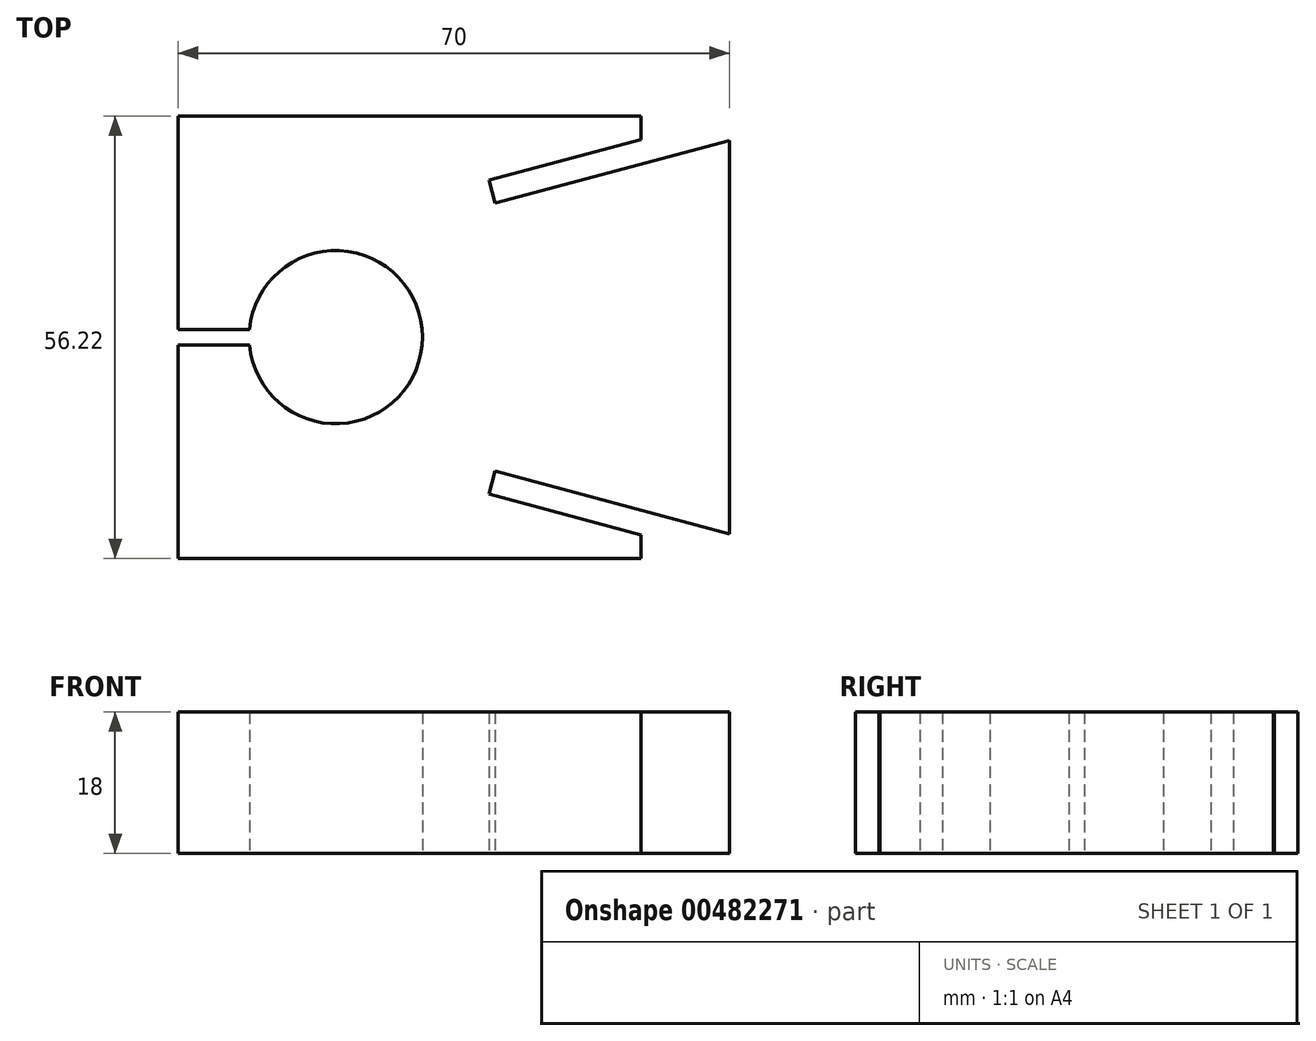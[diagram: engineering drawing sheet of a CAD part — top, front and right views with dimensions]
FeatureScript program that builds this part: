
annotation { "Feature Type Name" : "Feature", "Feature Type Description" : "" }
export const myFeature = defineFeature(function(context is Context, id is Id, definition is map)
    precondition{}
    {
        {
            var Q0;
            Q0=qCreatedBy(makeId("Top.planeOp"),FACE);
            var sketch = newSketch(context, id + "F0", { "sketchPlane" : qUnion([Q0])});
            skLineSegment(sketch, "E0", {"start": v(-70, 1) * mm, "end": v(-70, 28.1) * mm});
            skLineSegment(sketch, "E1", {"start": v(-70, 28.1) * mm, "end": v(-11.2, 28.1) * mm});
            skLineSegment(sketch, "E2", {"start": v(-11.2, 25.1) * mm, "end": v(-30.51, 19.93) * mm});
            skLineSegment(sketch, "E3", {"start": v(-30.51, 19.93) * mm, "end": v(-29.74, 17.03) * mm});
            skLineSegment(sketch, "E4", {"start": v(-29.74, 17.03) * mm, "end": v(0, 25) * mm});
            skLineSegment(sketch, "E5", {"start": v(0, 25) * mm, "end": v(0, 0) * mm});
            skLineSegment(sketch, "E6.MirrorCS", {"start": v(0, -25) * mm, "end": v(0, 0) * mm});
            skLineSegment(sketch, "E7.MirrorCS", {"start": v(-70, -1) * mm, "end": v(-70, -28.1) * mm});
            skLineSegment(sketch, "E8.MirrorCS", {"start": v(-29.74, -17.03) * mm, "end": v(0, -25) * mm});
            skLineSegment(sketch, "E9.MirrorCS", {"start": v(-70, -28.1) * mm, "end": v(-11.2, -28.1) * mm});
            skLineSegment(sketch, "E10.MirrorCS", {"start": v(-30.51, -19.93) * mm, "end": v(-29.74, -17.03) * mm});
            skLineSegment(sketch, "E11.MirrorCS", {"start": v(-11.2, -25.1) * mm, "end": v(-30.51, -19.93) * mm});
            skLineSegment(sketch, "E12", {"start": v(-11.2, 28.1) * mm, "end": v(-11.2, 25.1) * mm});
            skPoint(sketch, "E13.orphan", {"position": v(0, 28.1) * mm});
            skLineSegment(sketch, "E14.trimOffspring", {"start": v(-11.2, -25.1) * mm, "end": v(-11.2, -28.1) * mm});
            skPoint(sketch, "E15.orphan", {"position": v(0, -28.1) * mm});
            skArc(sketch, "E16", {"start": v(-60.95, -1) * mm, "mid": v(-39, 0) * mm, "end": v(-60.95, 1) * mm});
            skLineSegment(sketch, "E17.bottom", {"start": v(-60.95, 1) * mm, "end": v(-70, 1) * mm});
            skLineSegment(sketch, "E17.top", {"start": v(-60.95, -1) * mm, "end": v(-70, -1) * mm});
            skPoint(sketch, "E17.middle", {"position": v(-70, 0) * mm});
            skPoint(sketch, "E17.right.end.orphan", {"position": v(-79.05, -1) * mm});
            skPoint(sketch, "E17.right.start.orphan", {"position": v(-79.05, 1) * mm});
            skSolve(sketch);
        }
        {
            var Q0;
            Q0 = qSketchRegion(id + "F0", true);
            extrude(context, id + "F1", {"entities" : qUnion([Q0]), "depth" : 18 * mm});
        }
    });
